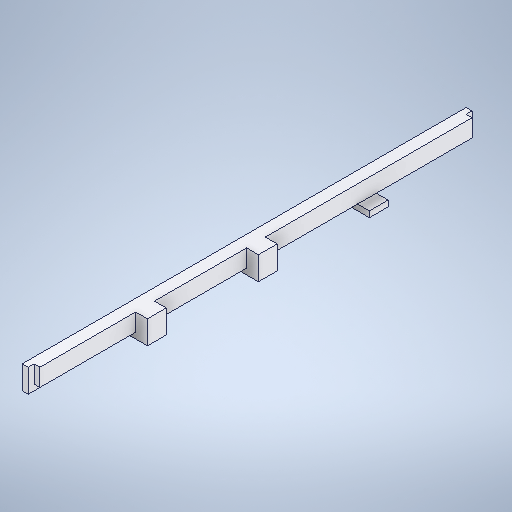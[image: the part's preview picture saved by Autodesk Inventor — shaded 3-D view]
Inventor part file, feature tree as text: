
AUTODESK INVENTOR PART (.ipt)
format: ipt  version: 2025 (Build 290162000, 162)  size: 472,576 bytes
history: native  units: in
note: dims shown in document units (in); Inventor stores cm internally (conversion verified against a paired STEP export)
features: projected_geometry x17, extrude x11, sketch x11
ambient origin geometry x8: Origin, YZ Plane, XZ Plane, XY Plane, X Axis, Y Axis, Z Axis, Center Point
bodies: Solid1 (feature_tree)
feature tree (39):
  extrude  "Extrusion1"  Depth=5.9213in
  extrude  "Extrusion2"  Depth=0.0787in
  extrude  "Extrusion3"  Depth=0.0787in
  extrude  "Extrusion4"  Depth=0.25in
  extrude  "Extrusion5"  Depth=0.25in
  extrude  "Extrusion6"  Depth=0.0787in TaperAngle=0.0deg
  extrude  "Extrusion10"  Depth=0.0787in
  extrude  "Extrusion11"  Depth=0.8in
  extrude  "Extrusion12"  Depth=0.25in
  extrude  "Extrusion13"  Depth=0.2362in
  extrude  "Extrusion14"  Depth=0.0787in
  sketch  "Sketch1"  dims[d0=2.75in d1=5.9213in]
  sketch  "Sketch2"  dims[d2=0.0787in d3=0.0in d4=0.0787in]
  projected_geometry  "Projected Loop1"
  sketch  "Sketch3"  dims[d5=0.0787in d6=0.0787in]
  projected_geometry  "Projected Loop2"
  sketch  "Sketch4"  dims[d7=0.0787in d8=0.0in d9=0.25in]
  projected_geometry  "Projected Loop3"
  sketch  "Sketch5"  dims[d10=0.25in d11=0.25in]
  projected_geometry  "Projected Loop4"
  sketch  "Sketch6"  dims[d12=0.1575in d13=0.0in d14=0.0787in d15=0.0in]
  projected_geometry  "Projected Loop5"
  projected_geometry  "Projected Loop6"
  projected_geometry  "Projected Loop7"
  projected_geometry  "Projected Loop8"
  sketch  "Sketch12"  dims[d16=0.0787in d17=0.0in d18=1.05in]
  projected_geometry  "Projected Loop12"
  projected_geometry  "Projected Loop13"
  sketch  "Sketch13"  dims[d22=1.3in d23=0.0in d31=0.8in]
  projected_geometry  "Projected Loop14"
  projected_geometry  "Projected Loop15"
  sketch  "Sketch14"  dims[d32=1.6in d33=0.25in]
  projected_geometry  "Projected Loop16"
  projected_geometry  "Projected Loop17"
  projected_geometry  "Projected Loop18"
  sketch  "Sketch15"  dims[d34=0.5in d35=0.2362in]
  projected_geometry  "Projected Loop19"
  projected_geometry  "Projected Loop20"
  sketch  "Sketch16"  dims[d36=0.25in d37=0.5in d38=0.2362in d39=0.1772in d40=0.1772in d41=0.1969in d42=0.0in d43=1.0in d44=0.0in d45=0.0787in d46=0.0in d47=0.1772in d48=0.1772in d49=0.1969in d50=0.0in d51=2.4375in d52=0.0in d29=0.5in d30=0.0344in]
